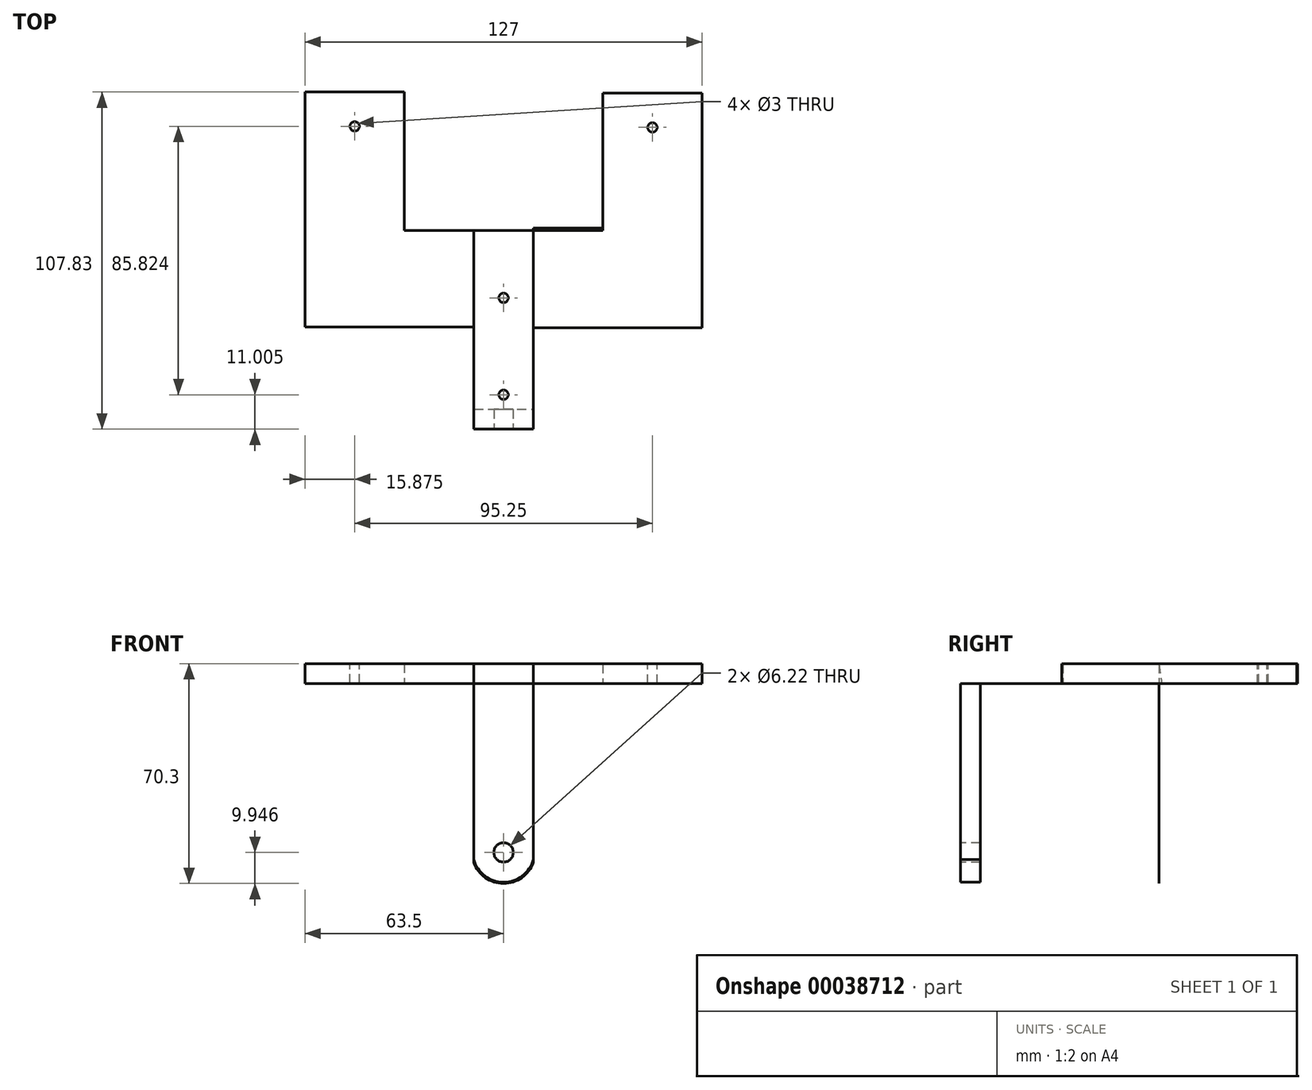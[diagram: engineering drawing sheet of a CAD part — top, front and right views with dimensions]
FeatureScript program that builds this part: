
annotation { "Feature Type Name" : "Feature", "Feature Type Description" : "" }
export const myFeature = defineFeature(function(context is Context, id is Id, definition is map)
    precondition{}
    {
        {
            var Q0;
            Q0=qCreatedBy(makeId("Front.planeOp"),FACE);
            var sketch = newSketch(context, id + "F0", { "sketchPlane" : qUnion([Q0])});
            skLineSegment(sketch, "E0", {"start": v(-9.53, 25.2) * mm, "end": v(9.53, 25.2) * mm});
            skLineSegment(sketch, "E1", {"start": v(9.53, 25.2) * mm, "end": v(9.53, -31.01) * mm});
            skLineSegment(sketch, "E2", {"start": v(-9.53, 25.2) * mm, "end": v(-9.53, -31.01) * mm});
            skArc(sketch, "E3", {"start": v(-9.53, -31.01) * mm, "mid": v(0, -38.3) * mm, "end": v(9.53, -31.01) * mm});
            skSolve(sketch);
        }
        {
            var Q0;
            Q0=qSketchRegion(id+"F0",true);
            extrude(context, id + "F1", {"entities" : qUnion([Q0]), "depth" : 3.17 * mm});
        }
        {
            var Q0;
            Q0=qSketchRegion(id+"F0",true);
            extrude(context, id + "F2", {"entities" : qUnion([Q0]), "operationType" : NewBodyOperationType.ADD, "oppositeDirection" : true, "depth" : 3.17 * mm});
        }
        {
            var Q0;
            Q0=qCreatedBy(makeId("Front.planeOp"),FACE);
            var sketch = newSketch(context, id + "F3", { "sketchPlane" : qUnion([Q0])});
            skCircle(sketch, "E4", {"center": v(0, -28.73) * mm, "radius": 3.11 * mm});
            skLineSegment(sketch, "E5", {"start": v(0, -28.73) * mm, "end": v(0, -38.26) * mm});
            skSolve(sketch);
        }
        {
            var Q0;
            Q0=qSketchRegion(id+"F3",true);
            extrude(context, id + "F4", {"entities" : qUnion([Q0]), "operationType" : NewBodyOperationType.REMOVE, "oppositeDirection" : true, "depth" : 25.4 * mm});
        }
        {
            var Q0;
            Q0=qSketchRegion(id+"F3",true);
            extrude(context, id + "F5", {"entities" : qUnion([Q0]), "operationType" : NewBodyOperationType.REMOVE, "depth" : 25.4 * mm});
        }
        {
            var Q0;
            {var subQ0=sQuery(id+"F0.wireOp",EDGE,"E0");Q0=makeQuery(id+"F2.boolean.opBoolean","MERGE",FACE,{"derivedFrom":[makeQuery(id+"F1.opExtrude","SWEPT_FACE",FACE,{"disambiguationData":[OSD([subQ0])]}),makeQuery(id+"F2.opExtrude","SWEPT_FACE",FACE,{"disambiguationData":[OSD([subQ0])]})]});}
            var sketch = newSketch(context, id + "F6", { "sketchPlane" : qUnion([Q0])});
            skLineSegment(sketch, "E6", {"start": v(-9.53, -3.18) * mm, "end": v(-9.53, 60.33) * mm});
            skPoint(sketch, "E7.endSnap0", {"position": v(9.53, 0) * mm});
            skLineSegment(sketch, "E8", {"start": v(9.53, -3.18) * mm, "end": v(9.53, 60.33) * mm});
            skLineSegment(sketch, "E9", {"start": v(9.53, 60.33) * mm, "end": v(-9.53, 60.33) * mm});
            skLineSegment(sketch, "E10", {"start": v(-9.53, -3.18) * mm, "end": v(9.53, -3.18) * mm});
            skSolve(sketch);
        }
        {
            var Q0;
            Q0=qSketchRegion(id+"F6",true);
            extrude(context, id + "F7", {"entities" : qUnion([Q0]), "operationType" : NewBodyOperationType.ADD, "depth" : 1 / 101.6 * mm});
        }
        {
            var Q0;
            Q0=makeQuery(id+"F7.opExtrude","SWEPT_FACE",FACE,{"disambiguationData":[OSD([sQuery(id+"F6.wireOp",EDGE,"E9")])]});
            var sketch = newSketch(context, id + "F8", { "sketchPlane" : qUnion([Q0])});
            skPoint(sketch, "E11.endSnap0", {"position": v(-9.53, 28.38) * mm});
            skArc(sketch, "E12", {"start": v(-9.53, -31.94) * mm, "mid": v(0, -38.68) * mm, "end": v(9.53, -31.94) * mm});
            skLineSegment(sketch, "E13", {"start": v(-9.53, 31.56) * mm, "end": v(-9.53, -31.94) * mm});
            skLineSegment(sketch, "E14", {"start": v(9.53, 31.56) * mm, "end": v(9.53, -31.94) * mm});
            skLineSegment(sketch, "E15", {"start": v(-9.53, 31.56) * mm, "end": v(9.53, 31.56) * mm});
            skSolve(sketch);
        }
        {
            var Q0;
            Q0=qSketchRegion(id+"F8",true);
            extrude(context, id + "F9", {"entities" : qUnion([Q0]), "oppositeDirection" : true, "depth" : 1 / 101.6 * mm});
        }
        {
            var Q0;
            Q0=qSketchRegion(id+"F3",true);
            extrude(context, id + "F10", {"entities" : qUnion([Q0]), "operationType" : NewBodyOperationType.REMOVE, "oppositeDirection" : true, "depth" : 2540 * mm});
        }
        {
            var Q0;
            Q0=makeQuery(id+"F7.opExtrude","CAP_FACE",FACE,{"disambiguationData":[OSD([sQuery(id+"F6.wireOp",EDGE,"E6"),sQuery(id+"F6.wireOp",EDGE,"E8"),sQuery(id+"F6.wireOp",EDGE,"E9"),sQuery(id+"F6.wireOp",EDGE,"E10")])],"isStart":false});
            var sketch = newSketch(context, id + "F11", { "sketchPlane" : qUnion([Q0])});
            skCircle(sketch, "E16", {"center": v(0, 7.82) * mm, "radius": 1.5 * mm});
            skCircle(sketch, "E17", {"center": v(0, 38.8) * mm, "radius": 1.5 * mm});
            skSolve(sketch);
        }
        {
            var Q0;
            Q0=qSketchRegion(id+"F11",true);
            extrude(context, id + "F12", {"entities" : qUnion([Q0]), "operationType" : NewBodyOperationType.REMOVE, "oppositeDirection" : true, "depth" : 25.4 * mm});
        }
        {
            var Q0;
            {var subQ0=sQuery(id+"F0.wireOp",EDGE,"E1");Q0=makeQuery(id+"F7.boolean.opBoolean","MERGE",FACE,{"derivedFrom":[makeQuery(id+"F2.boolean.opBoolean","MERGE",FACE,{"derivedFrom":[makeQuery(id+"F1.opExtrude","SWEPT_FACE",FACE,{"disambiguationData":[OSD([subQ0])]}),makeQuery(id+"F2.opExtrude","SWEPT_FACE",FACE,{"disambiguationData":[OSD([subQ0])]})]}),makeQuery(id+"F7.opExtrude","SWEPT_FACE",FACE,{"disambiguationData":[OSD([sQuery(id+"F6.wireOp",EDGE,"E8")])]})]});}
            var sketch = newSketch(context, id + "F13", { "sketchPlane" : qUnion([Q0])});
            skLineSegment(sketch, "E18", {"start": v(104.33, 31.56) * mm, "end": v(104.33, 25.2) * mm});
            skLineSegment(sketch, "E19", {"start": v(29.18, 31.56) * mm, "end": v(104.33, 31.56) * mm});
            skLineSegment(sketch, "E20", {"start": v(104.33, 25.2) * mm, "end": v(29.18, 25.2) * mm});
            skLineSegment(sketch, "E21", {"start": v(29.18, 25.2) * mm, "end": v(29.18, 31.56) * mm});
            skSolve(sketch);
        }
        {
            var Q0;
            Q0=qSketchRegion(id+"F13",true);
            extrude(context, id + "F14", {"entities" : qUnion([Q0]), "operationType" : NewBodyOperationType.ADD, "depth" : 53.97 * mm});
        }
        {
            var Q0;
            Q0=makeQuery(id+"F14.boolean.opBoolean","MERGE",FACE,{"derivedFrom":[makeQuery(id+"F9.opExtrude","SWEPT_FACE",FACE,{"disambiguationData":[OSD([sQuery(id+"F8.wireOp",EDGE,"E15")])]}),makeQuery(id+"F7.opExtrude","CAP_FACE",FACE,{"disambiguationData":[OSD([sQuery(id+"F6.wireOp",EDGE,"E6"),sQuery(id+"F6.wireOp",EDGE,"E8"),sQuery(id+"F6.wireOp",EDGE,"E9"),sQuery(id+"F6.wireOp",EDGE,"E10")])],"isStart":false}),makeQuery(id+"F14.opExtrude","SWEPT_FACE",FACE,{"disambiguationData":[OSD([sQuery(id+"F13.wireOp",EDGE,"7d0c347f-23ee-4703-af74-5e1430c4c102")])]})]});
            var sketch = newSketch(context, id + "F15", { "sketchPlane" : qUnion([Q0])});
            skCircle(sketch, "E22", {"center": v(47.62, 93.33) * mm, "radius": 1.5 * mm});
            skSolve(sketch);
        }
        {
            var Q0;
            Q0=qSketchRegion(id+"F15",true);
            extrude(context, id + "F16", {"entities" : qUnion([Q0]), "operationType" : NewBodyOperationType.REMOVE, "oppositeDirection" : true, "depth" : 25 * mm});
        }
        {
            var Q0;
            {var subQ0=sQuery(id+"F0.wireOp",EDGE,"E2");Q0=makeQuery(id+"F14.boolean.opBoolean","MERGE",FACE,{"derivedFrom":[makeQuery(id+"F7.boolean.opBoolean","MERGE",FACE,{"derivedFrom":[makeQuery(id+"F2.boolean.opBoolean","MERGE",FACE,{"derivedFrom":[makeQuery(id+"F1.opExtrude","SWEPT_FACE",FACE,{"disambiguationData":[OSD([subQ0])]}),makeQuery(id+"F2.opExtrude","SWEPT_FACE",FACE,{"disambiguationData":[OSD([subQ0])]})]}),makeQuery(id+"F7.opExtrude","SWEPT_FACE",FACE,{"disambiguationData":[OSD([sQuery(id+"F6.wireOp",EDGE,"E6")])]})]}),makeQuery(id+"F9.opExtrude","SWEPT_FACE",FACE,{"disambiguationData":[OSD([sQuery(id+"F8.wireOp",EDGE,"E14")])]})]});}
            var sketch = newSketch(context, id + "F17", { "sketchPlane" : qUnion([Q0])});
            skLineSegment(sketch, "E23", {"start": v(-104.65, 25.27) * mm, "end": v(-104.65, 31.62) * mm});
            skLineSegment(sketch, "E24", {"start": v(-104.65, 31.62) * mm, "end": v(-29.5, 31.62) * mm});
            skLineSegment(sketch, "E25", {"start": v(-29.5, 31.62) * mm, "end": v(-29.5, 25.27) * mm});
            skLineSegment(sketch, "E26", {"start": v(-29.5, 25.27) * mm, "end": v(-104.65, 25.27) * mm});
            skSolve(sketch);
        }
        {
            var Q0;
            Q0=qSketchRegion(id+"F17",true);
            var Q1;
            Q1=sQuery(id+"F17.wireOp",EDGE,"E23");
            var Q2;
            Q2=sQuery(id+"F17.wireOp",EDGE,"E24");
            var Q3;
            Q3=sQuery(id+"F17.wireOp",EDGE,"E25");
            var Q4;
            Q4=sQuery(id+"F17.wireOp",EDGE,"E26");
            extrude(context, id + "F18", {"entities" : qUnion([Q0]), "operationType" : NewBodyOperationType.ADD, "surfaceEntities" : qUnion([Q1, Q2, Q3, Q4]), "depth" : 53.97 * mm});
        }
        {
            var Q0;
            Q0=makeQuery(id+"F18.opExtrude","SWEPT_FACE",FACE,{"disambiguationData":[OSD([sQuery(id+"F17.wireOp",EDGE,"E24")])]});
            var sketch = newSketch(context, id + "F19", { "sketchPlane" : qUnion([Q0])});
            skCircle(sketch, "E27", {"center": v(-47.63, 93.65) * mm, "radius": 1.5 * mm});
            skSolve(sketch);
        }
        {
            var Q0;
            Q0=qSketchRegion(id+"F19",true);
            extrude(context, id + "F20", {"entities" : qUnion([Q0]), "operationType" : NewBodyOperationType.REMOVE, "oppositeDirection" : true, "depth" : 25 * mm});
        }
        {
            var Q0;
            Q0=makeQuery(id+"F14.opExtrude","CAP_FACE",FACE,{"disambiguationData":[OSD([sQuery(id+"F13.wireOp",EDGE,"E18"),sQuery(id+"F13.wireOp",EDGE,"E19"),sQuery(id+"F13.wireOp",EDGE,"E20"),sQuery(id+"F13.wireOp",EDGE,"E21")])],"isStart":true});
            var sketch = newSketch(context, id + "F21", { "sketchPlane" : qUnion([Q0])});
            skLineSegment(sketch, "E28", {"start": v(-104.33, 25.2) * mm, "end": v(-104.33, 31.56) * mm});
            skLineSegment(sketch, "E29", {"start": v(-104.33, 31.56) * mm, "end": v(-60.33, 31.56) * mm});
            skLineSegment(sketch, "E30", {"start": v(-60.33, 31.56) * mm, "end": v(-61.12, 25.2) * mm});
            skLineSegment(sketch, "E31", {"start": v(-61.12, 25.2) * mm, "end": v(-104.33, 25.2) * mm});
            skSolve(sketch);
        }
        {
            var Q0;
            Q0=qSketchRegion(id+"F21",true);
            extrude(context, id + "F22", {"entities" : qUnion([Q0]), "operationType" : NewBodyOperationType.REMOVE, "oppositeDirection" : true, "depth" : 22.22 * mm});
        }
        {
            var Q0;
            Q0=makeQuery(id+"F18.opExtrude","CAP_FACE",FACE,{"disambiguationData":[OSD([sQuery(id+"F17.wireOp",EDGE,"E23"),sQuery(id+"F17.wireOp",EDGE,"E24"),sQuery(id+"F17.wireOp",EDGE,"E25"),sQuery(id+"F17.wireOp",EDGE,"E26")])],"isStart":true});
            var sketch = newSketch(context, id + "F23", { "sketchPlane" : qUnion([Q0])});
            skLineSegment(sketch, "E32.bottom", {"start": v(104.65, 31.62) * mm, "end": v(60.33, 31.62) * mm});
            skLineSegment(sketch, "E32.top", {"start": v(104.65, 25.27) * mm, "end": v(60.33, 25.27) * mm});
            skLineSegment(sketch, "E32.left", {"start": v(104.65, 31.62) * mm, "end": v(104.65, 25.27) * mm});
            skLineSegment(sketch, "E32.right", {"start": v(60.33, 31.62) * mm, "end": v(60.33, 25.27) * mm});
            skSolve(sketch);
        }
        {
            var Q0;
            Q0=qSketchRegion(id+"F23",true);
            extrude(context, id + "F24", {"entities" : qUnion([Q0]), "operationType" : NewBodyOperationType.REMOVE, "oppositeDirection" : true, "depth" : 22.22 * mm});
        }
    });
